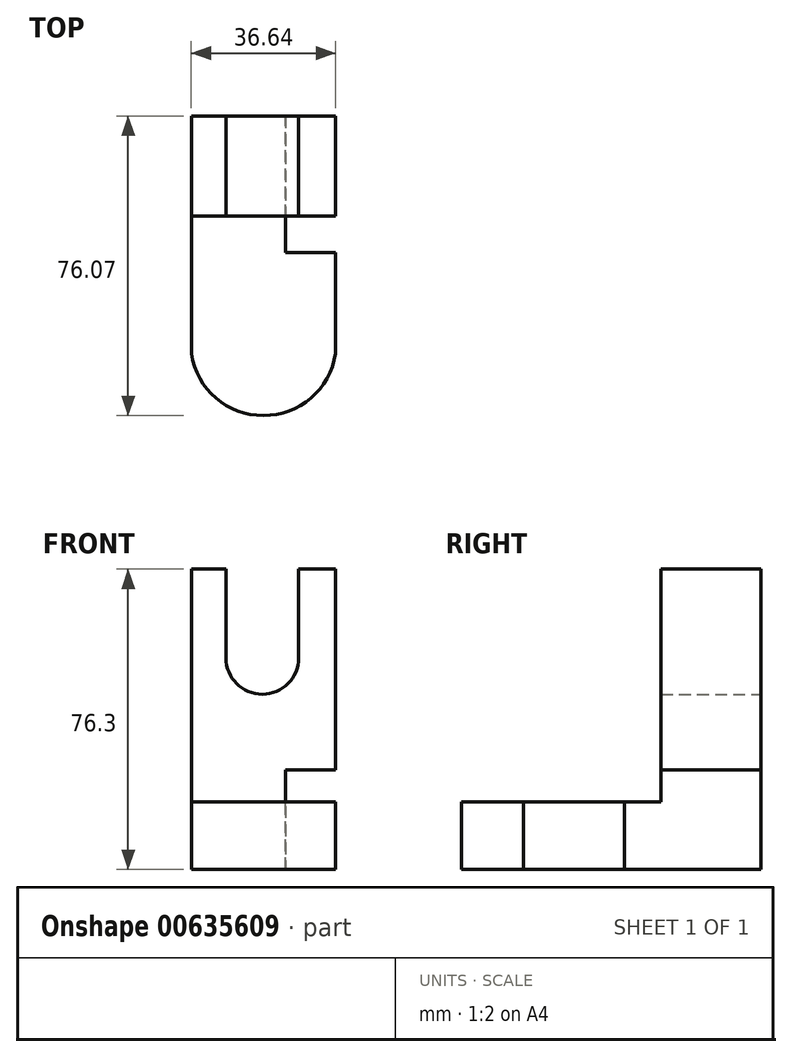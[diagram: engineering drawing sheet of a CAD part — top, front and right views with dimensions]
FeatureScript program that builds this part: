
annotation { "Feature Type Name" : "Feature", "Feature Type Description" : "" }
export const myFeature = defineFeature(function(context is Context, id is Id, definition is map)
    precondition{}
    {
        {
            var Q0;
            Q0=qCreatedBy(makeId("Front.planeOp"),FACE);
            var sketch = newSketch(context, id + "F0", { "sketchPlane" : qUnion([Q0])});
            skLineSegment(sketch, "E0.bottom", {"start": v(-18.32, 38.15) * mm, "end": v(-9.5, 38.15) * mm});
            skLineSegment(sketch, "E0.top", {"start": v(-18.32, -38.15) * mm, "end": v(18.32, -38.15) * mm});
            skLineSegment(sketch, "E0.left", {"start": v(-18.32, 38.15) * mm, "end": v(-18.32, -38.15) * mm});
            skLineSegment(sketch, "E0.right", {"start": v(18.32, 38.15) * mm, "end": v(18.32, -38.15) * mm});
            skPoint(sketch, "E0.middle", {"position": v(0, 0) * mm});
            skLineSegment(sketch, "E1.left", {"start": v(-9.5, 38.15) * mm, "end": v(-9.5, 15.56) * mm});
            skLineSegment(sketch, "E1.right", {"start": v(8.95, 38.15) * mm, "end": v(8.95, 15.56) * mm});
            skArc(sketch, "E2", {"start": v(-9.5, 15.56) * mm, "mid": v(-0.28, 6.33) * mm, "end": v(8.95, 15.56) * mm});
            skLineSegment(sketch, "E3.trimOffspring", {"start": v(8.95, 38.15) * mm, "end": v(18.32, 38.15) * mm});
            skSolve(sketch);
        }
        {
            var Q0;
            Q0=makeQuery(id+"F0.imprint","IMPRINT",FACE,{"disambiguationData":[TD([[makeQuery(id+"F0.imprint","IMPRINT",EDGE,{"derivedFrom":sQuery(id+"F0.wireOp",EDGE,"E0.bottom")}),-1.0]])]});
            extrude(context, id + "F1", {"entities" : qUnion([Q0]), "depth" : 25.4 * mm, "offsetDistance" : 25.4 * mm});
        }
        {
            var Q0;
            Q0=makeQuery(id+"F1.opExtrude","CAP_FACE",FACE,{"disambiguationData":[OSD([sQuery(id+"F0.wireOp",EDGE,"E0.bottom"),sQuery(id+"F0.wireOp",EDGE,"E0.top"),sQuery(id+"F0.wireOp",EDGE,"E0.left"),sQuery(id+"F0.wireOp",EDGE,"E0.right"),sQuery(id+"F0.wireOp",EDGE,"E1.left"),sQuery(id+"F0.wireOp",EDGE,"E1.right"),sQuery(id+"F0.wireOp",EDGE,"E2"),sQuery(id+"F0.wireOp",EDGE,"E3.trimOffspring")])],"isStart":false});
            var sketch = newSketch(context, id + "F2", { "sketchPlane" : qUnion([Q0])});
            skLineSegment(sketch, "E4.bottom", {"start": v(18.32, -38.15) * mm, "end": v(-18.32, -38.15) * mm});
            skLineSegment(sketch, "E4.top", {"start": v(18.32, -21.05) * mm, "end": v(-18.32, -21.05) * mm});
            skLineSegment(sketch, "E4.left", {"start": v(18.32, -38.15) * mm, "end": v(18.32, -21.05) * mm});
            skLineSegment(sketch, "E4.right", {"start": v(-18.32, -38.15) * mm, "end": v(-18.32, -21.05) * mm});
            skSolve(sketch);
        }
        {
            var Q0;
            Q0 = qSketchRegion(id + "F2", true);
            extrude(context, id + "F3", {"entities" : qUnion([Q0]), "operationType" : NewBodyOperationType.ADD, "depth" : 50.8 * mm, "offsetDistance" : 25.4 * mm});
        }
        {
            var Q0;
            Q0=makeQuery(id+"F3.opExtrude","SWEPT_FACE",FACE,{"disambiguationData":[OSD([sQuery(id+"F2.wireOp",EDGE,"E4.top")])]});
            var sketch = newSketch(context, id + "F4", { "sketchPlane" : qUnion([Q0])});
            skArc(sketch, "E5", {"start": v(-18.32, -54.72) * mm, "mid": v(0, -76.07) * mm, "end": v(18.32, -54.72) * mm});
            skSolve(sketch);
        }
        {
            var Q0;
            {var subQ1=sQuery(id+"F2.wireOp",EDGE,"E4.top");var subQ6=makeQuery(id+"F3.opExtrude","CAP_EDGE",EDGE,{"disambiguationData":[OSD([subQ1])],"isStart":false});Q0=makeQuery(id+"F4.imprint","IMPRINT",FACE,{"disambiguationData":[TD([[makeQuery(id+"F4.imprint","IMPRINT",EDGE,{"derivedFrom":subQ6}),-1.0]])]});}
            extrude(context, id + "F5", {"entities" : qUnion([Q0]), "operationType" : NewBodyOperationType.REMOVE, "endBound" : BoundingType.THROUGH_ALL, "oppositeDirection" : true, "depth" : 25.4 * mm, "offsetDistance" : 25.4 * mm});
        }
        {
            var Q0;
            Q0=makeQuery(id+"F3.boolean.opBoolean","MERGE",FACE,{"derivedFrom":[makeQuery(id+"F1.opExtrude","SWEPT_FACE",FACE,{"disambiguationData":[OSD([sQuery(id+"F0.wireOp",EDGE,"E0.right")])]}),makeQuery(id+"F3.opExtrude","SWEPT_FACE",FACE,{"disambiguationData":[OSD([sQuery(id+"F2.wireOp",EDGE,"E4.left")])]})]});
            var sketch = newSketch(context, id + "F6", { "sketchPlane" : qUnion([Q0])});
            skLineSegment(sketch, "E6.bottom", {"start": v(0, -38.15) * mm, "end": v(-34.68, -38.15) * mm});
            skLineSegment(sketch, "E6.top", {"start": v(0, -12.92) * mm, "end": v(-34.68, -12.92) * mm});
            skLineSegment(sketch, "E6.left", {"start": v(0, -38.15) * mm, "end": v(0, -12.92) * mm});
            skLineSegment(sketch, "E6.right", {"start": v(-34.68, -38.15) * mm, "end": v(-34.68, -12.92) * mm});
            skSolve(sketch);
        }
        {
            var Q0;
            Q0 = qSketchRegion(id + "F6", true);
            extrude(context, id + "F7", {"entities" : qUnion([Q0]), "operationType" : NewBodyOperationType.REMOVE, "oppositeDirection" : true, "depth" : 12.7 * mm, "offsetDistance" : 25.4 * mm});
        }
    });
